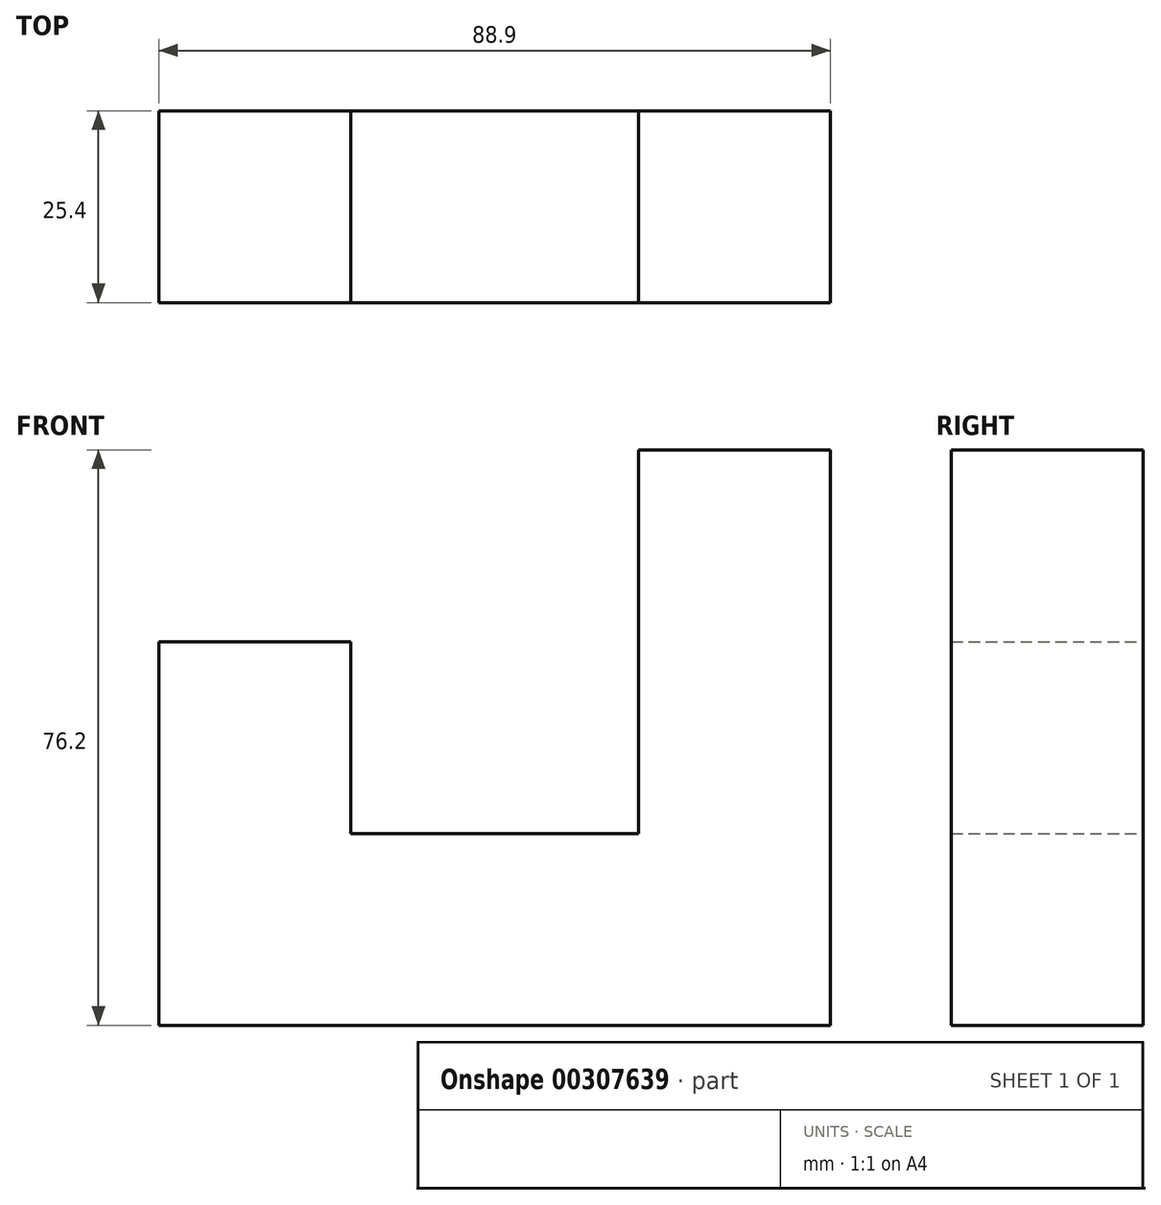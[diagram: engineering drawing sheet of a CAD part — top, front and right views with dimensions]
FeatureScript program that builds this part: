
annotation { "Feature Type Name" : "Feature", "Feature Type Description" : "" }
export const myFeature = defineFeature(function(context is Context, id is Id, definition is map)
    precondition{}
    {
        {
            var Q0;
            Q0=qCreatedBy(makeId("Front.planeOp"),FACE);
            var sketch = newSketch(context, id + "F0", { "sketchPlane" : qUnion([Q0])});
            skLineSegment(sketch, "E0", {"start": v(-35.4, -41.75) * mm, "end": v(53.5, -41.75) * mm});
            skLineSegment(sketch, "E1", {"start": v(53.5, -41.75) * mm, "end": v(53.5, 34.45) * mm});
            skLineSegment(sketch, "E2", {"start": v(53.5, 34.45) * mm, "end": v(28.1, 34.45) * mm});
            skLineSegment(sketch, "E3", {"start": v(28.1, 34.45) * mm, "end": v(28.1, -16.35) * mm});
            skLineSegment(sketch, "E4", {"start": v(28.1, -16.35) * mm, "end": v(-10, -16.35) * mm});
            skLineSegment(sketch, "E5", {"start": v(-10, -16.35) * mm, "end": v(-10, 9.05) * mm});
            skLineSegment(sketch, "E6", {"start": v(-10, 9.05) * mm, "end": v(-35.4, 9.05) * mm});
            skLineSegment(sketch, "E7", {"start": v(-35.4, 9.05) * mm, "end": v(-35.4, -41.75) * mm});
            skSolve(sketch);
        }
        {
            var Q0;
            Q0=makeQuery(id+"F0.imprint","IMPRINT",FACE,{"disambiguationData":[TD([[makeQuery(id+"F0.imprint","IMPRINT",EDGE,{"derivedFrom":sQuery(id+"F0.wireOp",EDGE,"E0")}),1.0]])]});
            extrude(context, id + "F1", {"entities" : qUnion([Q0]), "depth" : 25.4 * mm});
        }
    });
